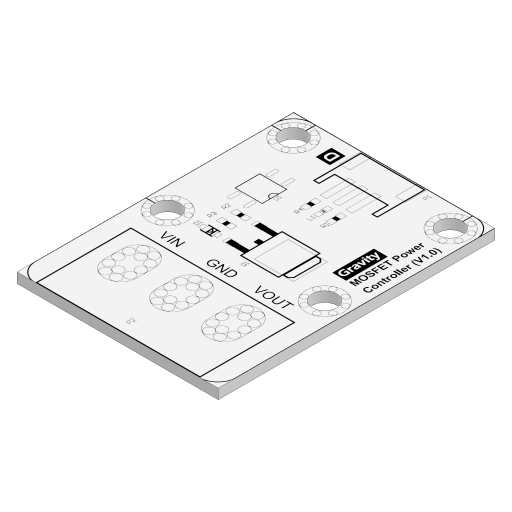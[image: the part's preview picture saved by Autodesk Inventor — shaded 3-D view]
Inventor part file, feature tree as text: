
AUTODESK INVENTOR PART (.ipt)
format: ipt  version: 2024.3 (Build 283343000, 343)  size: 1,433,088 bytes
history: native  units: mm
features: sketch x3, other x2, extrude x1, hole x1
ambient origin geometry x8: Origin, YZ Plane, XZ Plane, XY Plane, X Axis, Y Axis, Z Axis, Center Point
bodies: Solid1 (feature_tree)
feature tree (7):
  sketch  "Sketch1"  dims[d5=44.0mm d9=31.995493mm]
  extrude  "Extrusion1"  Depth=31.995493mm
  other  "Decal1"
  hole  "Hole1"  [1 undecoded]
  other  "Image1"
  sketch  "Sketch2"  dims[d10=1.6mm d11=0.0mm d14=25.0mm]
  sketch  "Sketch4"  dims[d15=20.0mm d16=3.9mm d17=6.0mm d18=4.4mm d19=2.0mm d20=90.0deg d21=3.0mm d22=0.0mm]
note: 1 required parameter value undecoded (feature->parameter linkage not recoverable at this tier; creation-order binding heuristic only, values carry confidence <= 0.55)
